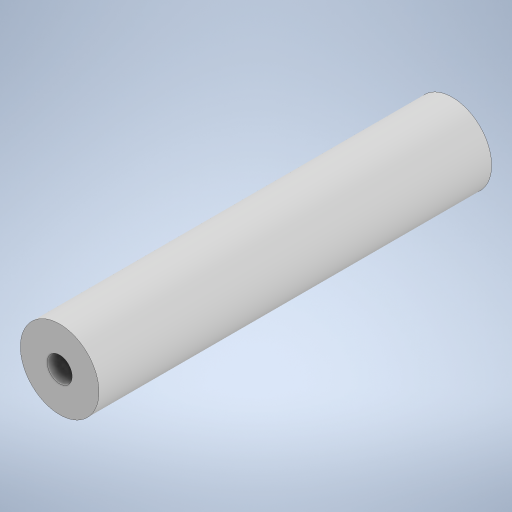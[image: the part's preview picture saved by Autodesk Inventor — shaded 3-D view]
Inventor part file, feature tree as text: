
AUTODESK INVENTOR PART (.ipt)
format: ipt  version: 2024 (Build 280153000, 153)  size: 232,960 bytes
history: native  units: in
note: dims shown in document units (in); Inventor stores cm internally (conversion verified against a paired STEP export)
features: extrude x3, sketch x3
ambient origin geometry x8: Origin, YZ Plane, XZ Plane, XY Plane, X Axis, Y Axis, Z Axis, Center Point
bodies: Solid1 (feature_tree)
feature tree (6):
  extrude  "Extrusion1"  Depth=3.937in TaperAngle=0.0deg
  extrude  "Extrusion2"  Depth=0.7874in TaperAngle=0.0deg
  extrude  "Extrusion3"  Depth=0.7874in TaperAngle=0.0deg
  sketch  "Sketch1"  dims[d0=0.7874in d1=3.937in d2=0.0in]
  sketch  "Sketch2"  dims[d3=0.25in d4=0.7874in d5=0.0in]
  sketch  "Sketch3"  dims[d6=0.25in d7=0.7874in d8=0.0in]
